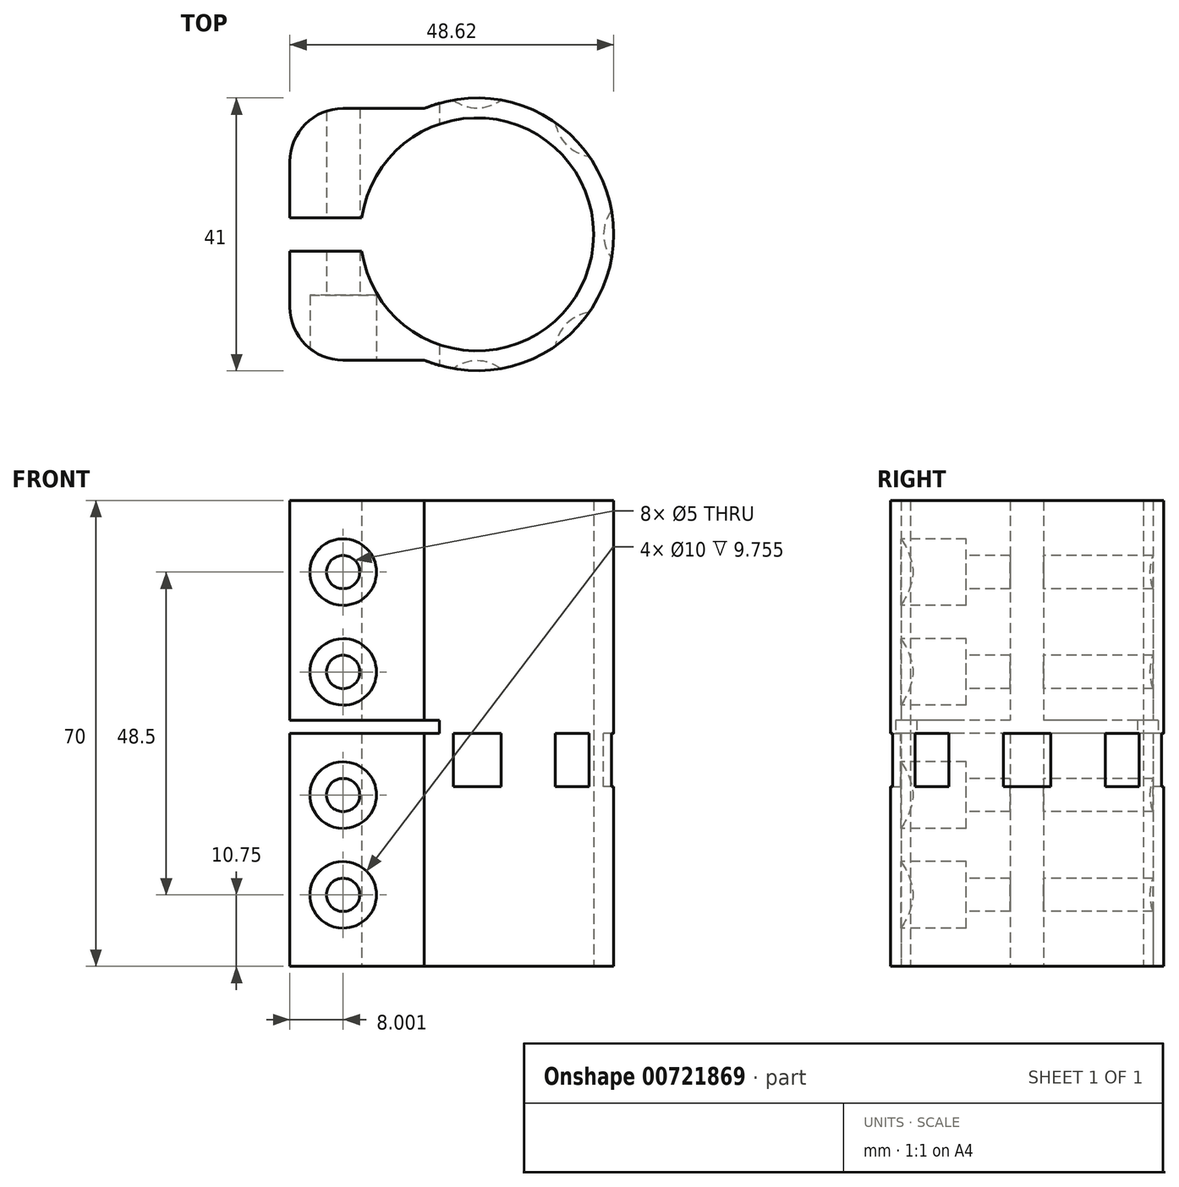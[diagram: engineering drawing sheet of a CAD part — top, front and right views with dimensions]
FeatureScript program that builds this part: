
annotation { "Feature Type Name" : "Feature", "Feature Type Description" : "" }
export const myFeature = defineFeature(function(context is Context, id is Id, definition is map)
    precondition{}
    {
        {
            var Q0;
            Q0=qCreatedBy(makeId("Top.planeOp"),FACE);
            var sketch = newSketch(context, id + "F0", { "sketchPlane" : qUnion([Q0])});
            skArc(sketch, "E0", {"start": v(-7.92, -18.9) * mm, "mid": v(20.5, 0) * mm, "end": v(-7.92, 18.9) * mm});
            skArc(sketch, "E1", {"start": v(-17.32, -2.5) * mm, "mid": v(17.5, 0) * mm, "end": v(-17.32, 2.5) * mm});
            skLineSegment(sketch, "E2", {"start": v(-7.92, 18.9) * mm, "end": v(-20.12, 18.9) * mm});
            skLineSegment(sketch, "E3", {"start": v(-28.12, 10.9) * mm, "end": v(-28.12, 2.5) * mm});
            skLineSegment(sketch, "E4", {"start": v(-28.12, 2.5) * mm, "end": v(-17.32, 2.5) * mm});
            skPoint(sketch, "E5.visualSharp", {"position": v(-28.12, 18.9) * mm});
            skArc(sketch, "E5.filletArc", {"start": v(-20.12, 18.9) * mm, "mid": v(-25.78, 16.57) * mm, "end": v(-28.12, 10.9) * mm});
            skLineSegment(sketch, "E6.MirrorCS", {"start": v(-28.12, -10.9) * mm, "end": v(-28.12, -2.5) * mm});
            skLineSegment(sketch, "E7.MirrorCS", {"start": v(-7.92, -18.9) * mm, "end": v(-20.12, -18.9) * mm});
            skLineSegment(sketch, "E8.MirrorCS", {"start": v(-28.12, -2.5) * mm, "end": v(-17.32, -2.5) * mm});
            skArc(sketch, "E9.MirrorCS", {"start": v(-20.12, -18.9) * mm, "mid": v(-25.78, -16.57) * mm, "end": v(-28.12, -10.9) * mm});
            skSolve(sketch);
        }
        {
            var Q0;
            Q0 = qSketchRegion(id + "F0", true);
            extrude(context, id + "F1", {"entities" : qUnion([Q0]), "endBound" : BoundingType.SYMMETRIC, "depth" : 70 * mm, "offsetDistance" : 25 * mm});
        }
        {
            var Q0;
            Q0=makeQuery(id+"F1.opExtrude","SWEPT_FACE",FACE,{"disambiguationData":[OSD([sQuery(id+"F0.wireOp",EDGE,"E7.MirrorCS")])]});
            var sketch = newSketch(context, id + "F2", { "sketchPlane" : qUnion([Q0])});
            skLineSegment(sketch, "E10", {"start": v(-20.12, 24.25) * mm, "end": v(-20.12, 9.25) * mm});
            skLineSegment(sketch, "E11", {"start": v(-20.12, -24.25) * mm, "end": v(-20.12, -9.25) * mm});
            skLineSegment(sketch, "E12", {"start": v(-20.12, -9.25) * mm, "end": v(-20.12, 9.25) * mm});
            skLineSegment(sketch, "E13", {"start": v(0.08, 9.25) * mm, "end": v(0.08, 0) * mm});
            skSolve(sketch);
        }
        {
            var Q0;
            Q0=sQuery(id+"F2.wireOp",VERTEX,"E11.start");
            var Q1;
            Q1=sQuery(id+"F2.wireOp",VERTEX,"E11.end");
            var Q2;
            Q2=sQuery(id+"F2.wireOp",VERTEX,"E10.end");
            var Q3;
            Q3=sQuery(id+"F2.wireOp",VERTEX,"E10.start");
            var Q4;
            Q4=makeQuery(id+"F1.opExtrude","SWEPT_BODY",BODY,{"disambiguationData":[OSD([sQuery(id+"F0.wireOp",EDGE,"E0"),sQuery(id+"F0.wireOp",EDGE,"E1"),sQuery(id+"F0.wireOp",EDGE,"E2"),sQuery(id+"F0.wireOp",EDGE,"E3"),sQuery(id+"F0.wireOp",EDGE,"E4"),sQuery(id+"F0.wireOp",EDGE,"E5.filletArc"),sQuery(id+"F0.wireOp",EDGE,"E6.MirrorCS"),sQuery(id+"F0.wireOp",EDGE,"E7.MirrorCS"),sQuery(id+"F0.wireOp",EDGE,"E8.MirrorCS"),sQuery(id+"F0.wireOp",EDGE,"E9.MirrorCS")])]});
            hole(context, id + "F3", {"style" : HoleStyle.C_BORE, "endStyle" : HoleEndStyle.THROUGH, "holeDiameter" : 5 * mm, "cBoreDiameter" : 10 * mm, "cBoreDepth" : 8 * mm, "majorDiameter" : 5 * mm, "isTappedThrough" : true, "tappedDepth" : 12 * mm, "tapClearance" : 3, "locations" : qUnion([Q0, Q1, Q2, Q3]), "scope" : qUnion([Q4])});
        }
        {
            var Q0;
            Q0=qCreatedBy(makeId("Front.planeOp"),FACE);
            var sketch = newSketch(context, id + "F4", { "sketchPlane" : qUnion([Q0])});
            skLineSegment(sketch, "E14.bottom", {"start": v(-5.64, 0) * mm, "end": v(-28.12, 0) * mm});
            skLineSegment(sketch, "E14.top", {"start": v(-5.64, 2) * mm, "end": v(-28.12, 2) * mm});
            skLineSegment(sketch, "E14.left", {"start": v(-5.64, 0) * mm, "end": v(-5.64, 2) * mm});
            skLineSegment(sketch, "E14.right", {"start": v(-28.12, 0) * mm, "end": v(-28.12, 2) * mm});
            skSolve(sketch);
        }
        {
            var Q0;
            Q0 = qSketchRegion(id + "F4", true);
            extrude(context, id + "F5", {"entities" : qUnion([Q0]), "operationType" : NewBodyOperationType.REMOVE, "endBound" : BoundingType.SYMMETRIC, "oppositeDirection" : true, "depth" : 50 * mm, "offsetDistance" : 25 * mm});
        }
        {
            var Q0;
            Q0=qCreatedBy(makeId("Top.planeOp"),FACE);
            var sketch = newSketch(context, id + "F6", { "sketchPlane" : qUnion([Q0])});
            skCircle(sketch, "E15", {"center": v(0, -25) * mm, "radius": 6 * mm});
            skCircle(sketch, "E16.1.0", {"center": v(17.68, -17.68) * mm, "radius": 6 * mm});
            skCircle(sketch, "E16.2.0", {"center": v(25, 0) * mm, "radius": 6 * mm});
            skCircle(sketch, "E16.3.0", {"center": v(17.68, 17.68) * mm, "radius": 6 * mm});
            skCircle(sketch, "E16.4.0", {"center": v(0, 25) * mm, "radius": 6 * mm});
            skPoint(sketch, "E16.center", {"position": v(0, 0) * mm});
            skLineSegment(sketch, "E16.anchor1", {"start": v(0, 0) * mm, "end": v(0, -25) * mm, "construction": true});
            skLineSegment(sketch, "E16.anchor2", {"start": v(0, 0) * mm, "end": v(0, 25) * mm, "construction": true});
            skSolve(sketch);
        }
        {
            var Q0;
            Q0 = qSketchRegion(id + "F6", true);
            extrude(context, id + "F7", {"entities" : qUnion([Q0]), "operationType" : NewBodyOperationType.REMOVE, "oppositeDirection" : true, "depth" : 8 * mm, "offsetDistance" : 25 * mm});
        }
    });
